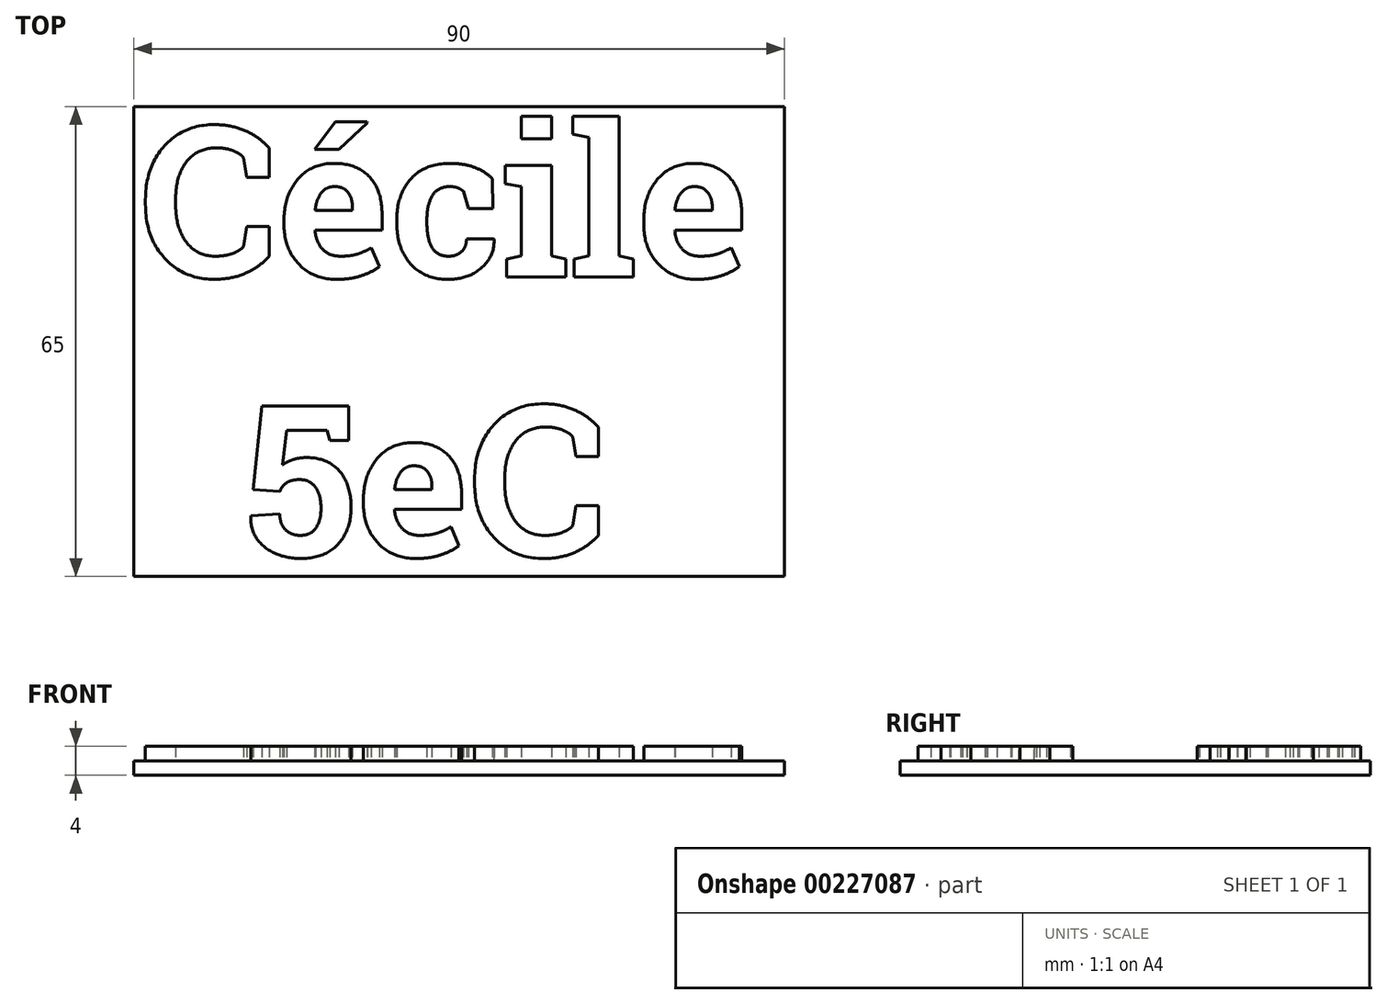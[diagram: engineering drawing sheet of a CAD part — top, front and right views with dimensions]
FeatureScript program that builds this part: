
annotation { "Feature Type Name" : "Feature", "Feature Type Description" : "" }
export const myFeature = defineFeature(function(context is Context, id is Id, definition is map)
    precondition{}
    {
        {
            var Q0;
            Q0=qCreatedBy(makeId("Top.planeOp"),FACE);
            var sketch = newSketch(context, id + "F0", { "sketchPlane" : qUnion([Q0])});
            skLineSegment(sketch, "E0.bottom", {"start": v(0, 0) * mm, "end": v(90, 0) * mm});
            skLineSegment(sketch, "E0.top", {"start": v(0, -65) * mm, "end": v(90, -65) * mm});
            skLineSegment(sketch, "E0.left", {"start": v(0, 0) * mm, "end": v(0, -65) * mm});
            skLineSegment(sketch, "E0.right", {"start": v(90, 0) * mm, "end": v(90, -65) * mm});
            skSolve(sketch);
        }
        {
            var Q0;
            Q0 = qSketchRegion(id + "F0", true);
            extrude(context, id + "F1", {"entities" : qUnion([Q0]), "depth" : 2 * mm});
        }
        {
            var Q0;
            Q0=makeQuery(id+"F1.opExtrude","CAP_FACE",FACE,{"disambiguationData":[OSD([sQuery(id+"F0.wireOp",EDGE,"E0.bottom"),sQuery(id+"F0.wireOp",EDGE,"E0.top"),sQuery(id+"F0.wireOp",EDGE,"E0.left"),sQuery(id+"F0.wireOp",EDGE,"E0.right")])],"isStart":false});
            var sketch = newSketch(context, id + "F2", { "sketchPlane" : qUnion([Q0])});
            skSolve(sketch);
        }
        {
            var Q0;
            Q0=makeQuery(id+"F2.imprint","IMPRINT",FACE,{"disambiguationData":[TD([[makeQuery(id+"F2.imprint","IMPRINT",EDGE,{"derivedFrom":makeQuery(id+"F1.opExtrude","CAP_EDGE",EDGE,{"disambiguationData":[OSD([sQuery(id+"F0.wireOp",EDGE,"E0.bottom")])],"isStart":false})}),-1.0]])]});
            var sketch = newSketch(context, id + "F3", { "sketchPlane" : qUnion([Q0])});
            skText(sketch, "E1", { "text": "Cécile\n  5eC", "fontName": "RobotoSlab-Bold.ttf"});
            const initialGuessF3  = {"E1": [0.00089, -0.02361, 1, 0, 0.02106]};
            skSetInitialGuess(sketch, initialGuessF3);
            skSolve(sketch);
        }
        {
            var Q0;
            Q0 = qSketchRegion(id + "F3", true);
            extrude(context, id + "F4", {"entities" : qUnion([Q0]), "operationType" : NewBodyOperationType.ADD, "depth" : 2 * mm});
        }
    });
